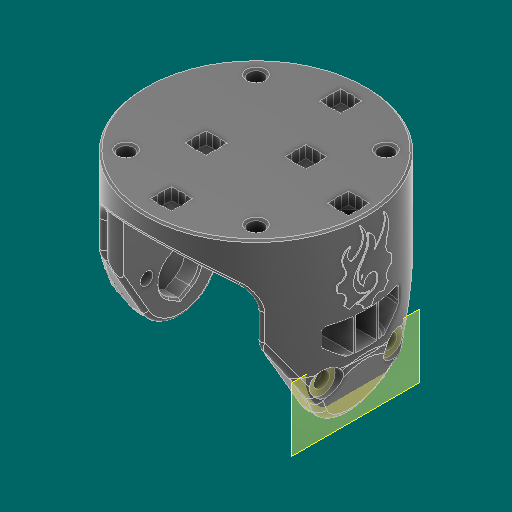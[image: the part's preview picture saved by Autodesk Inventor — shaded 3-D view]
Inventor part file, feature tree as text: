
AUTODESK INVENTOR PART (.ipt)
format: ipt  version: 2023.1 (Build 271208000, 208)  size: 4,671,488 bytes
history: native  units: in
note: dims shown in document units (in); Inventor stores cm internally (conversion verified against a paired STEP export)
features: extrude x17, sketch x15, other x11, chamfer x8, plane x7, fillet x6, projected_geometry x5, mirror x2, split x2, surface_op x1, pattern_circular x1
ambient origin geometry x8: Origin, YZ Plane, XZ Plane, XY Plane, X Axis, Y Axis, Z Axis, Center Point
bodies: Solid1 (feature_tree), Solid2 (feature_tree), Solid3 (feature_tree), Solid4 (feature_tree), Solid5 (feature_tree)
feature tree (75):
  sketch  "Sketch2"  dims[d11=1.2362in d15=2.75in]
  extrude  "Extrusion1"  Depth=2.75in
  plane  "Work Plane1"
  extrude  "Extrusion2"  TaperAngle=45.0deg  [1 undecoded]
  extrude  "Extrusion4"  Depth=1.5748in TaperAngle=360.0deg
  extrude  "Extrusion5"  Depth=0.26in
  fillet  "Fillet2"  Radius=3.0in
  fillet  "Fillet3"  Radius=0.05in
  extrude  "Extrusion11"  Depth=0.05in
  fillet  "Fillet7"  Radius=0.26in
  fillet  "Fillet4"  Radius=0.26in
  fillet  "Fillet5"  Radius=0.26in
  sketch  "Sketch6"  dims[d42=0.26in d43=0.26in d45=3.0in d46=0.05in]
  extrude  "Extrusion6"  Depth=0.7874in TaperAngle=360.0deg
  extrude  "Extrusion7"  Depth=2.75in
  extrude  "Extrusion8"  Depth=0.1in
  plane  "Work Plane4"
  extrude  "Extrusion9"  Depth=0.15in TaperAngle=0.0deg
  extrude  "Extrusion10"  Depth=0.5in
  chamfer  "Chamfer1"  [1 undecoded]
  chamfer  "Chamfer2"  Distance=0.1in
  fillet  "Fillet6"  Radius=0.05in
  chamfer  "Chamfer3"  Distance=3.1437in
  mirror  "Mirror1"
  chamfer  "Chamfer4"  Distance=0.25in
  other  "Ruled Surface1"
  surface_op  "Extend1"
  split  "Split1"
  sketch  "Sketch13"  dims[d65=1.875in d66=0.0in d74=0.0in d75=0.15in d76=0.0in]
  extrude  "Extrusion12"  Depth=0.1in
  plane  "Work Plane5"
  plane  "Work Plane8"
  extrude  "Extrusion13"  Depth=0.1in TaperAngle=0.0deg
  extrude  "Extrusion14"  Depth=0.1in TaperAngle=0.0deg
  chamfer  "Chamfer5"  Distance=0.19in
  split  "Split2"
  pattern_circular  "Circular Pattern1"  Count=4 Angle=360.0deg
  chamfer  "Chamfer6"  Distance=1.0in
  sketch  "Sketch16"  dims[d79=0.25in]
  extrude  "Extrusion15"  Depth=0.1in TaperAngle=0.0deg
  mirror  "Mirror2"
  chamfer  "Chamfer7"  Distance=1.0in
  chamfer  "Chamfer8"  Distance=0.4in
  plane  "Work Plane6"
  extrude  "Extrusion16"  Depth=0.1in
  extrude  "Extrusion17"  Depth=0.1in
  sketch  "Sketch3"  dims[d16=0.8661in d17=45.0deg]
  other  "Work Axis1"
  plane  "Work Plane2"
  sketch  "Sketch5"  dims[d18=0.4724in d35=1.5748in d37=360.0deg]
  sketch  "Sketch7"  dims[d48=0.05in d49=0.05in d50=0.26in d51=0.26in d52=0.26in]
  other  "Work Axis2"
  plane  "Work Plane3"
  sketch  "Sketch8"  dims[d53=0.26in d54=0.7874in d56=360.0deg]
  sketch  "Sketch9"  dims[d58=1.775in d59=0.75in d60=0.0in d61=0.0in d62=2.75in]
  sketch  "Sketch11"  dims[d63=0.1181in d64=0.1in]
  sketch  "3D Sketch2"
  other  "Srf1"
  sketch  "Sketch14"  dims[d77=0.3436in d78=0.5in]
  other  "Srf2"
  sketch  "Sketch17"  dims[d80=30.0deg d81=0.0in d82=0.0in]
  sketch  "Sketch18"  dims[d83=0.375in]
  projected_geometry  "Projected Loop1"
  projected_geometry  "Projected Loop2"
  projected_geometry  "Projected Loop3"
  projected_geometry  "Projected Loop4"
  sketch  "Sketch19"  dims[d84=0.1in d85=0.1in d86=0.05in d87=3.1437in d88=0.25in d89=0.51in d90=0.196in d91=0.0in d92=1.25in d93=0.0in d94=0.19in d95=1.5748in d97=360.0deg d99=1.0in d100=0.0in d101=0.0in d102=0.75in d103=1.0in d104=0.4in d105=0.0in d106=0.26in d107=0.26in d108=0.25in d109=0.0in d110=0.1875in d111=0.125in d112=45.0deg d113=0.1875in d114=0.125in d115=45.0deg d116=0.0472in d117=0.0236in d118=0.125in d119=45.0deg d120=0.275in d121=0.0236in d122=0.125in d123=45.0deg d124=0.196in d125=0.75in d126=0.0in d127=0.0in d128=0.25in d129=1.0in d130=0.0in d131=0.875in d132=0.875in d133=0.19in d134=0.3279in d135=1.0in d136=0.0in d138=1.0in d139=0.0in d140=0.1562in d141=1.0in d142=0.0in d143=0.0236in d144=0.125in d145=45.0deg d146=0.0in d147=0.0in d148=0.7874in d149=360.0deg d151=0.0236in d152=0.125in d153=45.0deg d154=0.0394in d180=0.0118in d181=0.0in d182=0.9in d183=0.698in d192=0.05in d193=0.05in d194=0.0236in d195=0.125in d196=45.0deg d197=0.0236in d198=0.125in d199=45.0deg d200=-0.25in d201=0.33in d202=0.0in d203=0.0in d204=60.0deg d205=0.0276in d206=0.0276in d207=0.196in d208=0.0in d210=0.1in d68=0.0in d69=0.0in d70=0.0in d71=0.0in d209=0.5in d211=0.5in d212=0.0344in]
  projected_geometry  "Projected Loop5"
  other  "<userpath>\Documents\CAD\guardSwerve5\MainAssy.iam"
  other  "MainAssy.iam"
  other  "WheelHalf:1"
  other  "WheelHalf_MIR:1"
  extrude  "ExtrusionSrf1"  Depth=0.1in TaperAngle=0.0deg
  other  "Bevel Gears:1"
  other  "Bevel Gear2:1"
note: 2 required parameter values undecoded (feature->parameter linkage not recoverable at this tier; creation-order binding heuristic only, values carry confidence <= 0.55)
